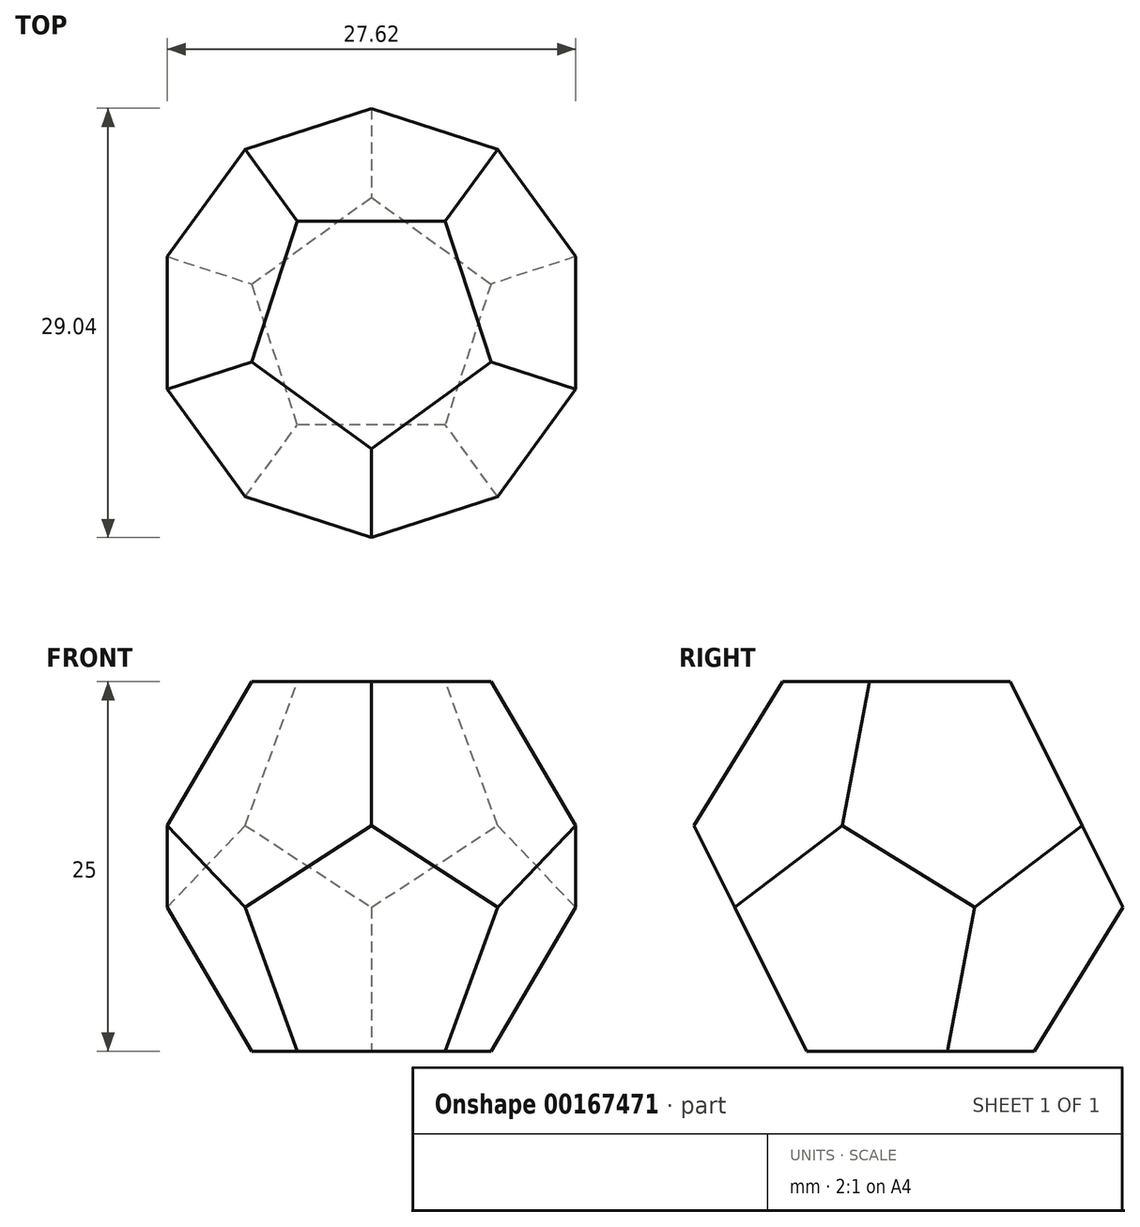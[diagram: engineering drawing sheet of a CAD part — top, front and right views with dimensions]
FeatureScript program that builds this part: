
annotation { "Feature Type Name" : "Feature", "Feature Type Description" : "" }
export const myFeature = defineFeature(function(context is Context, id is Id, definition is map)
    precondition{}
    {
        {
            var Q0;
            Q0=qCreatedBy(makeId("Top.planeOp"),FACE);
            var sketch = newSketch(context, id + "F0", { "sketchPlane" : qUnion([Q0])});
            skCircle(sketch, "E0.cCircle", {"center": v(0, 0) * mm, "radius": 6.88 * mm, "construction": true});
            skLineSegment(sketch, "E0.0", {"start": v(0, 8.5) * mm, "end": v(8.1, 2.63) * mm});
            skLineSegment(sketch, "E0.1", {"start": v(8.1, 2.63) * mm, "end": v(5, -6.88) * mm});
            skLineSegment(sketch, "E0.2", {"start": v(5, -6.88) * mm, "end": v(-5, -6.88) * mm});
            skLineSegment(sketch, "E0.3", {"start": v(-5, -6.88) * mm, "end": v(-8.1, 2.63) * mm});
            skLineSegment(sketch, "E0.4", {"start": v(-8.1, 2.63) * mm, "end": v(0, 8.5) * mm});
            skPoint(sketch, "E0.0.midPoint", {"position": v(4.05, 5.57) * mm});
            skSolve(sketch);
        }
        {
            var Q0;
            Q0=makeQuery(id+"F0.imprint","IMPRINT",FACE,{"disambiguationData":[TD([[makeQuery(id+"F0.imprint","IMPRINT",EDGE,{"derivedFrom":sQuery(id+"F0.wireOp",EDGE,"E0.0")}),-1.0]])]});
            extrude(context, id + "F1", {"entities" : qUnion([Q0]), "depth" : 25 * mm, "hasDraft" : true, "draftAngle" : acos(-1 / sqrt(5)) - 90 * degree});
        }
        {
            var Q0;
            Q0=makeQuery(id+"F1.opExtrude","CAP_FACE",FACE,{"disambiguationData":[OSD([sQuery(id+"F0.wireOp",EDGE,"E0.0"),sQuery(id+"F0.wireOp",EDGE,"E0.1"),sQuery(id+"F0.wireOp",EDGE,"E0.2"),sQuery(id+"F0.wireOp",EDGE,"E0.3"),sQuery(id+"F0.wireOp",EDGE,"E0.4")])],"isStart":false});
            var sketch = newSketch(context, id + "F2", { "sketchPlane" : qUnion([Q0])});
            skCircle(sketch, "E1.cCircle", {"center": v(0, 0) * mm, "radius": 6.88 * mm, "construction": true});
            skLineSegment(sketch, "E1.0", {"start": v(5, 6.88) * mm, "end": v(8.1, -2.63) * mm});
            skLineSegment(sketch, "E1.1", {"start": v(8.1, -2.63) * mm, "end": v(0, -8.5) * mm});
            skLineSegment(sketch, "E1.2", {"start": v(0, -8.5) * mm, "end": v(-8.1, -2.63) * mm});
            skLineSegment(sketch, "E1.3", {"start": v(-8.1, -2.63) * mm, "end": v(-5, 6.88) * mm});
            skLineSegment(sketch, "E1.4", {"start": v(-5, 6.88) * mm, "end": v(5, 6.88) * mm});
            skPoint(sketch, "E1.0.midPoint", {"position": v(6.55, 2.13) * mm});
            skSolve(sketch);
        }
        {
            var Q0;
            Q0=makeQuery(id+"F2.imprint","IMPRINT",FACE,{"disambiguationData":[TD([[makeQuery(id+"F2.imprint","IMPRINT",EDGE,{"derivedFrom":sQuery(id+"F2.wireOp",EDGE,"E1.0")}),1.0]])]});
            extrude(context, id + "F3", {"entities" : qUnion([Q0]), "operationType" : NewBodyOperationType.REMOVE, "oppositeDirection" : true, "depth" : 51.1 * mm, "hasDraft" : true, "draftAngle" : acos(-1 / sqrt(5)) - 90 * degree, "draftPullDirection" : true});
        }
    });
